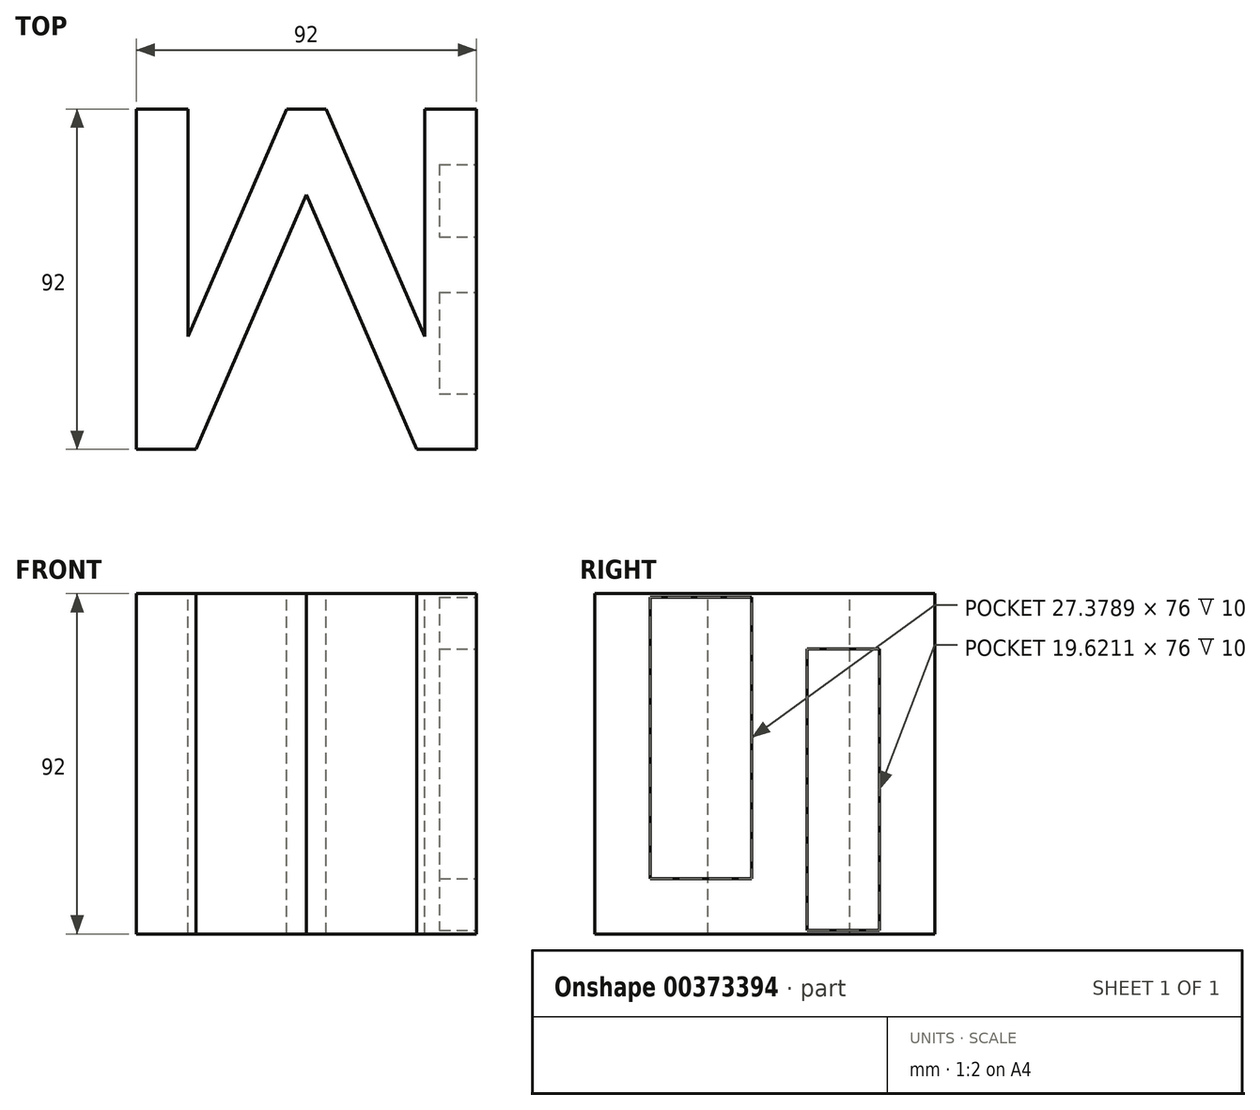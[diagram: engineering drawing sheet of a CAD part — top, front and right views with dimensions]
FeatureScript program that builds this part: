
annotation { "Feature Type Name" : "Feature", "Feature Type Description" : "" }
export const myFeature = defineFeature(function(context is Context, id is Id, definition is map)
    precondition{}
    {
        {
            var Q0;
            Q0=qCreatedBy(makeId("Top.planeOp"),FACE);
            var sketch = newSketch(context, id + "F0", { "sketchPlane" : qUnion([Q0])});
            skLineSegment(sketch, "E0", {"start": v(-46, -46.6) * mm, "end": v(-46, 45.4) * mm});
            skLineSegment(sketch, "E1", {"start": v(-46, 45.4) * mm, "end": v(-32, 45.4) * mm});
            skLineSegment(sketch, "E2", {"start": v(-32, 45.4) * mm, "end": v(-32, -16.07) * mm});
            skLineSegment(sketch, "E3", {"start": v(-32, -16.07) * mm, "end": v(-5.37, 45.4) * mm});
            skLineSegment(sketch, "E4", {"start": v(-5.37, 45.4) * mm, "end": v(0, 45.4) * mm});
            skLineSegment(sketch, "E5", {"start": v(-46, -46.6) * mm, "end": v(-29.85, -46.6) * mm});
            skLineSegment(sketch, "E6", {"start": v(-29.85, -46.6) * mm, "end": v(0, 22.31) * mm});
            skLineSegment(sketch, "E7.MirrorCS", {"start": v(32, 45.4) * mm, "end": v(32, -16.07) * mm});
            skLineSegment(sketch, "E8.MirrorCS", {"start": v(5.37, 45.4) * mm, "end": v(0, 45.4) * mm});
            skLineSegment(sketch, "E9.MirrorCS", {"start": v(32, -16.07) * mm, "end": v(5.37, 45.4) * mm});
            skLineSegment(sketch, "E10.MirrorCS", {"start": v(46, -46.6) * mm, "end": v(46, 45.4) * mm});
            skLineSegment(sketch, "E11.MirrorCS", {"start": v(29.85, -46.6) * mm, "end": v(0, 22.31) * mm});
            skLineSegment(sketch, "E12.MirrorCS", {"start": v(46, -46.6) * mm, "end": v(29.85, -46.6) * mm});
            skLineSegment(sketch, "E13.MirrorCS", {"start": v(46, 45.4) * mm, "end": v(32, 45.4) * mm});
            skSolve(sketch);
        }
        {
            var Q0;
            Q0 = qSketchRegion(id + "F0", true);
            extrude(context, id + "F1", {"entities" : qUnion([Q0]), "oppositeDirection" : true, "depth" : 92 * mm});
        }
        {
            var Q0;
            Q0=makeQuery(id+"F1.opExtrude","SWEPT_FACE",FACE,{"disambiguationData":[OSD([sQuery(id+"F0.wireOp",EDGE,"E10.MirrorCS")])]});
            var sketch = newSketch(context, id + "F2", { "sketchPlane" : qUnion([Q0])});
            skLineSegment(sketch, "E14.top", {"start": v(30.4, -15) * mm, "end": v(10.78, -15) * mm});
            skLineSegment(sketch, "E15.top", {"start": v(-4.22, -77) * mm, "end": v(-31.6, -77) * mm});
            skLineSegment(sketch, "E15.left", {"start": v(-4.22, -1) * mm, "end": v(-4.22, -77) * mm});
            skLineSegment(sketch, "E15.right", {"start": v(-31.6, -1) * mm, "end": v(-31.6, -77) * mm});
            skLineSegment(sketch, "E16", {"start": v(-31.6, -1) * mm, "end": v(-4.22, -1) * mm});
            skLineSegment(sketch, "E17", {"start": v(30.4, -15) * mm, "end": v(30.4, -91) * mm});
            skLineSegment(sketch, "E18", {"start": v(30.4, -91) * mm, "end": v(10.78, -91) * mm});
            skLineSegment(sketch, "E19", {"start": v(10.78, -91) * mm, "end": v(10.78, -15) * mm});
            skLineSegment(sketch, "E20", {"start": v(45.4, -46) * mm, "end": v(30.4, -46) * mm, "construction": true});
            skLineSegment(sketch, "E21", {"start": v(30.4, -46) * mm, "end": v(10.78, -46) * mm, "construction": true});
            skLineSegment(sketch, "E22", {"start": v(10.78, -46) * mm, "end": v(-4.22, -46) * mm, "construction": true});
            skLineSegment(sketch, "E23", {"start": v(-4.22, -46) * mm, "end": v(-31.6, -46) * mm, "construction": true});
            skLineSegment(sketch, "E24", {"start": v(-31.6, -46) * mm, "end": v(-46.6, -46) * mm, "construction": true});
            skLineSegment(sketch, "E25", {"start": v(20.59, -15) * mm, "end": v(20.59, 0) * mm, "construction": true});
            skLineSegment(sketch, "E26", {"start": v(-17.91, -77) * mm, "end": v(-17.91, -92) * mm, "construction": true});
            skSolve(sketch);
        }
        {
            var Q0;
            Q0 = qSketchRegion(id + "F2", true);
            extrude(context, id + "F3", {"entities" : qUnion([Q0]), "operationType" : NewBodyOperationType.REMOVE, "oppositeDirection" : true, "depth" : 10 * mm});
        }
    });
